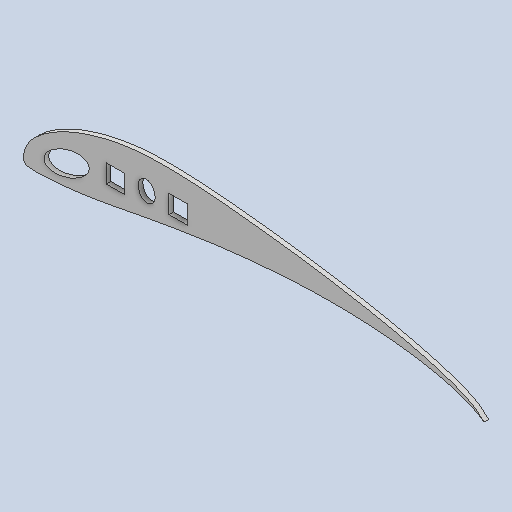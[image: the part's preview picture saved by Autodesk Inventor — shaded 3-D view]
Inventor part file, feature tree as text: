
AUTODESK INVENTOR PART (.ipt)
format: ipt  version: 2024 (Build 280153000, 153)  size: 126,976 bytes
history: native  units: in
note: dims shown in document units (in); Inventor stores cm internally (conversion verified against a paired STEP export)
features: other x3, sketch x1
ambient origin geometry x8: Origin, YZ Plane, XZ Plane, XY Plane, X Axis, Y Axis, Z Axis, Center Point
bodies: Solid1 (feature_tree)
feature tree (4):
  other  "new air foil.ipt"
  other  "Solid1::new air foil.ipt"
  other  "TaggingFeature1"
  sketch  "Sketch1"  dims[d0=0.3937in]
